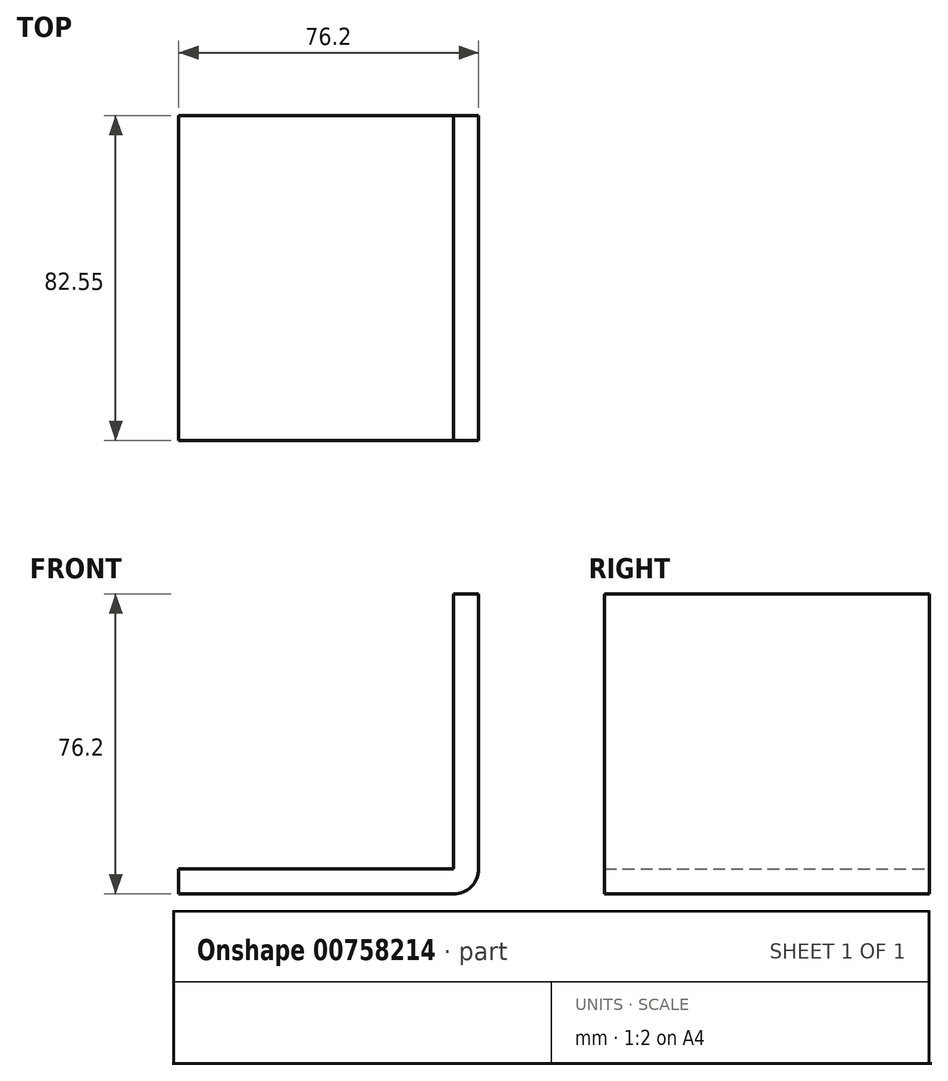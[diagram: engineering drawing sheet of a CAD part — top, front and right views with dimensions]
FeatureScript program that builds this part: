
annotation { "Feature Type Name" : "Feature", "Feature Type Description" : "" }
export const myFeature = defineFeature(function(context is Context, id is Id, definition is map)
    precondition{}
    {
        {
            var Q0;
            Q0=qCreatedBy(makeId("Top.planeOp"),FACE);
            var sketch = newSketch(context, id + "F0", { "sketchPlane" : qUnion([Q0])});
            skLineSegment(sketch, "E0.bottom", {"start": v(0, 0) * mm, "end": v(69.85, 0) * mm});
            skLineSegment(sketch, "E0.top", {"start": v(0, 82.55) * mm, "end": v(69.85, 82.55) * mm});
            skLineSegment(sketch, "E0.left", {"start": v(0, 0) * mm, "end": v(0, 82.55) * mm});
            skLineSegment(sketch, "E0.right", {"start": v(69.85, 0) * mm, "end": v(69.85, 82.55) * mm});
            skSolve(sketch);
        }
        {
            var Q0;
            Q0=makeQuery(id+"F0.imprint","IMPRINT",FACE,{"disambiguationData":[TD([[makeQuery(id+"F0.imprint","IMPRINT",EDGE,{"derivedFrom":sQuery(id+"F0.wireOp",EDGE,"E0.bottom")}),1.0]])]});
            extrude(context, id + "F1", {"entities" : qUnion([Q0]), "depth" : 6.35 * mm, "offsetDistance" : 25.4 * mm});
        }
        {
            var Q0;
            Q0=makeQuery(id+"F1.opExtrude","SWEPT_FACE",FACE,{"disambiguationData":[OSD([sQuery(id+"F0.wireOp",EDGE,"E0.right")])]});
            var sketch = newSketch(context, id + "F2", { "sketchPlane" : qUnion([Q0])});
            skLineSegment(sketch, "E1.bottom", {"start": v(0, 6.35) * mm, "end": v(82.55, 6.35) * mm});
            skLineSegment(sketch, "E1.top", {"start": v(0, 0) * mm, "end": v(82.55, 0) * mm});
            skLineSegment(sketch, "E1.left", {"start": v(0, 6.35) * mm, "end": v(0, 0) * mm});
            skLineSegment(sketch, "E1.right", {"start": v(82.55, 6.35) * mm, "end": v(82.55, 0) * mm});
            skSolve(sketch);
        }
        {
            var Q0;
            Q0=makeQuery(id+"F2.imprint","IMPRINT",FACE,{"disambiguationData":[TD([[makeQuery(id+"F2.imprint","IMPRINT",EDGE,{"derivedFrom":sQuery(id+"F2.wireOp",EDGE,"E1.bottom")}),-1.0]])]});
            var Q1;
            Q1=sQuery(id+"F2.wireOp",EDGE,"E1.bottom");
            revolve(context, id + "F3", {"operationType" : NewBodyOperationType.ADD, "surfaceOperationType" : NewSurfaceOperationType.NEW, "entities" : qUnion([Q0]), "axis" : qUnion([Q1]), "revolveType" : RevolveType.ONE_DIRECTION, "oppositeDirection" : true, "angle" : 90 * degree});
        }
        {
            var Q0;
            Q0=makeQuery(id+"F3.boolean.opBoolean","MERGE",FACE,{"derivedFrom":[makeQuery(id+"F1.opExtrude","CAP_FACE",FACE,{"disambiguationData":[OSD([sQuery(id+"F0.wireOp",EDGE,"E0.bottom"),sQuery(id+"F0.wireOp",EDGE,"E0.top"),sQuery(id+"F0.wireOp",EDGE,"E0.left"),sQuery(id+"F0.wireOp",EDGE,"E0.right")])],"isStart":false}),makeQuery(id+"F3.opRevolve","CAP_FACE",FACE,{"disambiguationData":[OSD([sQuery(id+"F2.wireOp",EDGE,"E1.bottom"),sQuery(id+"F2.wireOp",EDGE,"E1.top"),sQuery(id+"F2.wireOp",EDGE,"E1.left"),sQuery(id+"F2.wireOp",EDGE,"E1.right")])],"isStart":false})]});
            var sketch = newSketch(context, id + "F4", { "sketchPlane" : qUnion([Q0])});
            skLineSegment(sketch, "E2.bottom", {"start": v(76.2, 82.55) * mm, "end": v(69.85, 82.55) * mm});
            skLineSegment(sketch, "E2.top", {"start": v(76.2, 0) * mm, "end": v(69.85, 0) * mm});
            skLineSegment(sketch, "E2.left", {"start": v(76.2, 82.55) * mm, "end": v(76.2, 0) * mm});
            skLineSegment(sketch, "E2.right", {"start": v(69.85, 82.55) * mm, "end": v(69.85, 0) * mm});
            skSolve(sketch);
        }
        {
            var Q0;
            Q0=makeQuery(id+"F4.imprint","IMPRINT",FACE,{"disambiguationData":[TD([[makeQuery(id+"F4.imprint","IMPRINT",EDGE,{"derivedFrom":sQuery(id+"F4.wireOp",EDGE,"E2.bottom")}),-1.0]])]});
            extrude(context, id + "F5", {"entities" : qUnion([Q0]), "operationType" : NewBodyOperationType.ADD, "depth" : 69.85 * mm, "offsetDistance" : 25.4 * mm});
        }
    });
